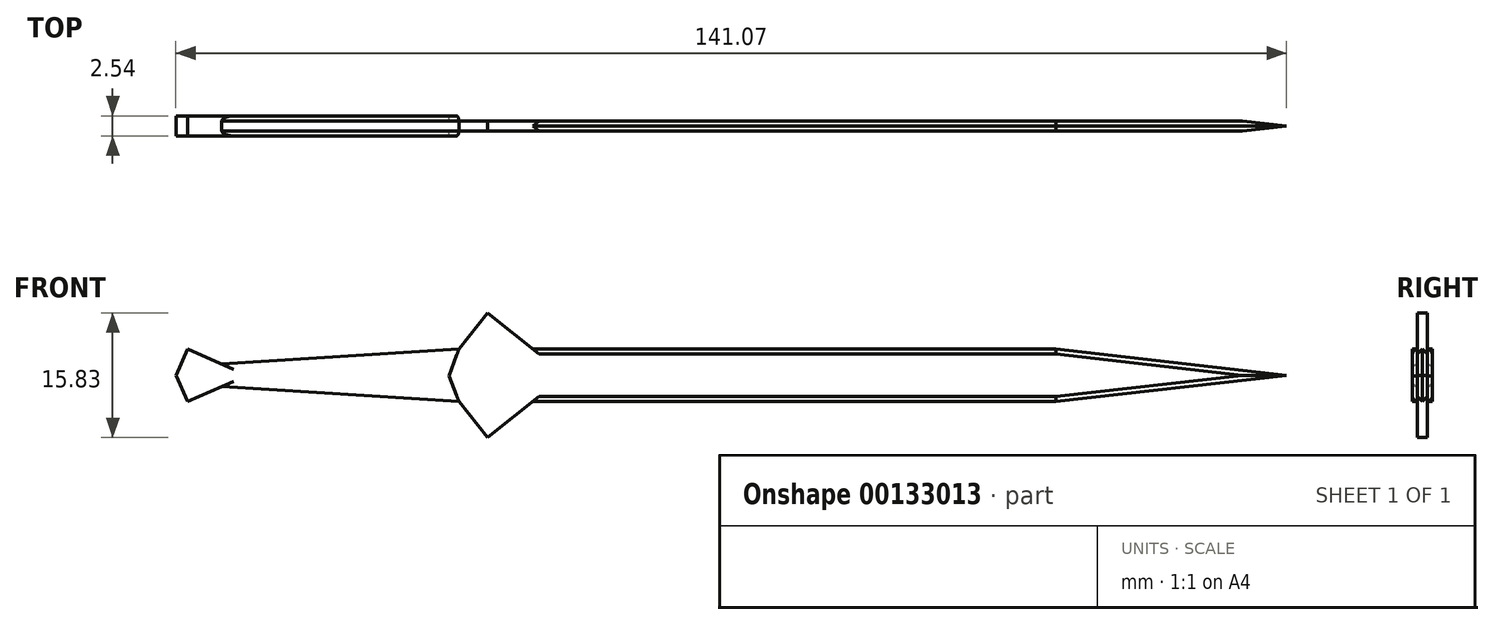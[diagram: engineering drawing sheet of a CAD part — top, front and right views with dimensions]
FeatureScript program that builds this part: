
annotation { "Feature Type Name" : "Feature", "Feature Type Description" : "" }
export const myFeature = defineFeature(function(context is Context, id is Id, definition is map)
    precondition{}
    {
        {
            var Q0;
            Q0=qCreatedBy(makeId("Front.planeOp"),FACE);
            var sketch = newSketch(context, id + "F0", { "sketchPlane" : qUnion([Q0])});
            skLineSegment(sketch, "E0", {"start": v(0, 0) * mm, "end": v(-30.17, -1.9) * mm});
            skLineSegment(sketch, "E1", {"start": v(-30.17, -1.9) * mm, "end": v(-34.49, 0) * mm});
            skLineSegment(sketch, "E2", {"start": v(0, 0) * mm, "end": v(3.65, 4.58) * mm});
            skLineSegment(sketch, "E3", {"start": v(3.65, 4.58) * mm, "end": v(9.4, 0) * mm});
            skLineSegment(sketch, "E4", {"start": v(9.4, 0) * mm, "end": v(75.85, 0) * mm});
            skLineSegment(sketch, "E5", {"start": v(75.85, 0) * mm, "end": v(105.1, -3.34) * mm});
            skLineSegment(sketch, "E6", {"start": v(-34.49, 0) * mm, "end": v(-35.96, -3.34) * mm});
            skLineSegment(sketch, "E7.MirrorCS", {"start": v(9.4, -6.67) * mm, "end": v(75.85, -6.67) * mm});
            skLineSegment(sketch, "E8.MirrorCS", {"start": v(75.85, -6.67) * mm, "end": v(105.1, -3.34) * mm});
            skLineSegment(sketch, "E9.MirrorCS", {"start": v(3.65, -11.25) * mm, "end": v(9.4, -6.67) * mm});
            skLineSegment(sketch, "E10.MirrorCS", {"start": v(0, -6.67) * mm, "end": v(3.65, -11.25) * mm});
            skLineSegment(sketch, "E11.MirrorCS", {"start": v(0, -6.67) * mm, "end": v(-30.17, -4.78) * mm});
            skLineSegment(sketch, "E12.MirrorCS", {"start": v(-30.17, -4.78) * mm, "end": v(-34.49, -6.67) * mm});
            skLineSegment(sketch, "E13.MirrorCS", {"start": v(-34.49, -6.67) * mm, "end": v(-35.96, -3.34) * mm});
            skLineSegment(sketch, "E14", {"start": v(0, 0) * mm, "end": v(-1.28, -3.42) * mm});
            skLineSegment(sketch, "E15", {"start": v(0, -6.67) * mm, "end": v(-1.28, -3.42) * mm});
            skLineSegment(sketch, "E16", {"start": v(-35.96, -3.34) * mm, "end": v(-30.95, -3.34) * mm});
            skLineSegment(sketch, "E17", {"start": v(-30.95, -3.34) * mm, "end": v(-30.17, -1.9) * mm});
            skLineSegment(sketch, "E18", {"start": v(-30.17, -4.78) * mm, "end": v(-30.95, -3.34) * mm});
            skLineSegment(sketch, "E19", {"start": v(-30.95, -3.34) * mm, "end": v(-1.28, -3.42) * mm});
            skLineSegment(sketch, "E20", {"start": v(-1.28, -3.42) * mm, "end": v(105.1, -3.34) * mm});
            skSolve(sketch);
        }
        {
            var Q0;
            Q0=makeQuery(id+"F0.imprint","IMPRINT",FACE,{"disambiguationData":[TD([[makeQuery(id+"F0.imprint","IMPRINT",EDGE,{"derivedFrom":sQuery(id+"F0.wireOp",EDGE,"E1")}),1.0]])]});
            var Q1;
            Q1=makeQuery(id+"F0.imprint","IMPRINT",FACE,{"disambiguationData":[TD([[makeQuery(id+"F0.imprint","IMPRINT",EDGE,{"derivedFrom":sQuery(id+"F0.wireOp",EDGE,"E12.MirrorCS")}),-1.0]])]});
            var Q2;
            Q2=makeQuery(id+"F0.imprint","IMPRINT",FACE,{"disambiguationData":[TD([[makeQuery(id+"F0.imprint","IMPRINT",EDGE,{"derivedFrom":sQuery(id+"F0.wireOp",EDGE,"E0")}),1.0]])]});
            var Q3;
            Q3=makeQuery(id+"F0.imprint","IMPRINT",FACE,{"disambiguationData":[TD([[makeQuery(id+"F0.imprint","IMPRINT",EDGE,{"derivedFrom":sQuery(id+"F0.wireOp",EDGE,"E11.MirrorCS")}),-1.0]])]});
            extrude(context, id + "F1", {"entities" : qUnion([Q0, Q1, Q2, Q3]), "endBound" : BoundingType.SYMMETRIC, "depth" : 2.54 * mm});
        }
        {
            var Q0;
            Q0=makeQuery(id+"F1.opExtrude","CAP_EDGE",EDGE,{"disambiguationData":[OSD([sQuery(id+"F0.wireOp",EDGE,"E0")])],"isStart":false});
            var Q1;
            Q1=makeQuery(id+"F1.opExtrude","CAP_EDGE",EDGE,{"disambiguationData":[OSD([sQuery(id+"F0.wireOp",EDGE,"E0")])],"isStart":true});
            var Q2;
            Q2=makeQuery(id+"F1.opExtrude","CAP_EDGE",EDGE,{"disambiguationData":[OSD([sQuery(id+"F0.wireOp",EDGE,"E11.MirrorCS")])],"isStart":true});
            var Q3;
            Q3=makeQuery(id+"F1.opExtrude","CAP_EDGE",EDGE,{"disambiguationData":[OSD([sQuery(id+"F0.wireOp",EDGE,"E11.MirrorCS")])],"isStart":false});
            fillet(context, id + "F2", {"entities" : qUnion([Q0, Q1, Q2, Q3]), "radius" : 0.76 * mm, "tangentPropagation" : true, "allowEdgeOverflow" : false});
        }
        {
            var Q0;
            Q0 = qSketchRegion(id + "F0", true);
            extrude(context, id + "F3", {"entities" : qUnion([Q0]), "operationType" : NewBodyOperationType.ADD, "endBound" : BoundingType.SYMMETRIC, "depth" : 1.27 * mm});
        }
        {
            var Q0;
            Q0=makeQuery(id+"F3.opExtrude","CAP_EDGE",EDGE,{"disambiguationData":[OSD([sQuery(id+"F0.wireOp",EDGE,"E7.MirrorCS")])],"isStart":false});
            var Q1;
            Q1=makeQuery(id+"F3.opExtrude","CAP_EDGE",EDGE,{"disambiguationData":[OSD([sQuery(id+"F0.wireOp",EDGE,"E7.MirrorCS")])],"isStart":true});
            var Q2;
            Q2=makeQuery(id+"F3.opExtrude","CAP_EDGE",EDGE,{"disambiguationData":[OSD([sQuery(id+"F0.wireOp",EDGE,"E4")])],"isStart":false});
            var Q3;
            Q3=makeQuery(id+"F3.opExtrude","CAP_EDGE",EDGE,{"disambiguationData":[OSD([sQuery(id+"F0.wireOp",EDGE,"E4")])],"isStart":true});
            var Q4;
            Q4=makeQuery(id+"F3.opExtrude","CAP_EDGE",EDGE,{"disambiguationData":[OSD([sQuery(id+"F0.wireOp",EDGE,"E5")])],"isStart":false});
            var Q5;
            Q5=makeQuery(id+"F3.opExtrude","CAP_EDGE",EDGE,{"disambiguationData":[OSD([sQuery(id+"F0.wireOp",EDGE,"E5")])],"isStart":true});
            var Q6;
            Q6=makeQuery(id+"F3.opExtrude","CAP_EDGE",EDGE,{"disambiguationData":[OSD([sQuery(id+"F0.wireOp",EDGE,"E8.MirrorCS")])],"isStart":false});
            var Q7;
            Q7=makeQuery(id+"F3.opExtrude","CAP_EDGE",EDGE,{"disambiguationData":[OSD([sQuery(id+"F0.wireOp",EDGE,"E8.MirrorCS")])],"isStart":true});
            chamfer(context, id + "F4", {"entities" : qUnion([Q0, Q1, Q2, Q3, Q4, Q5, Q6, Q7]), "width" : 0.64 * mm, "tangentPropagation" : true});
        }
    });
